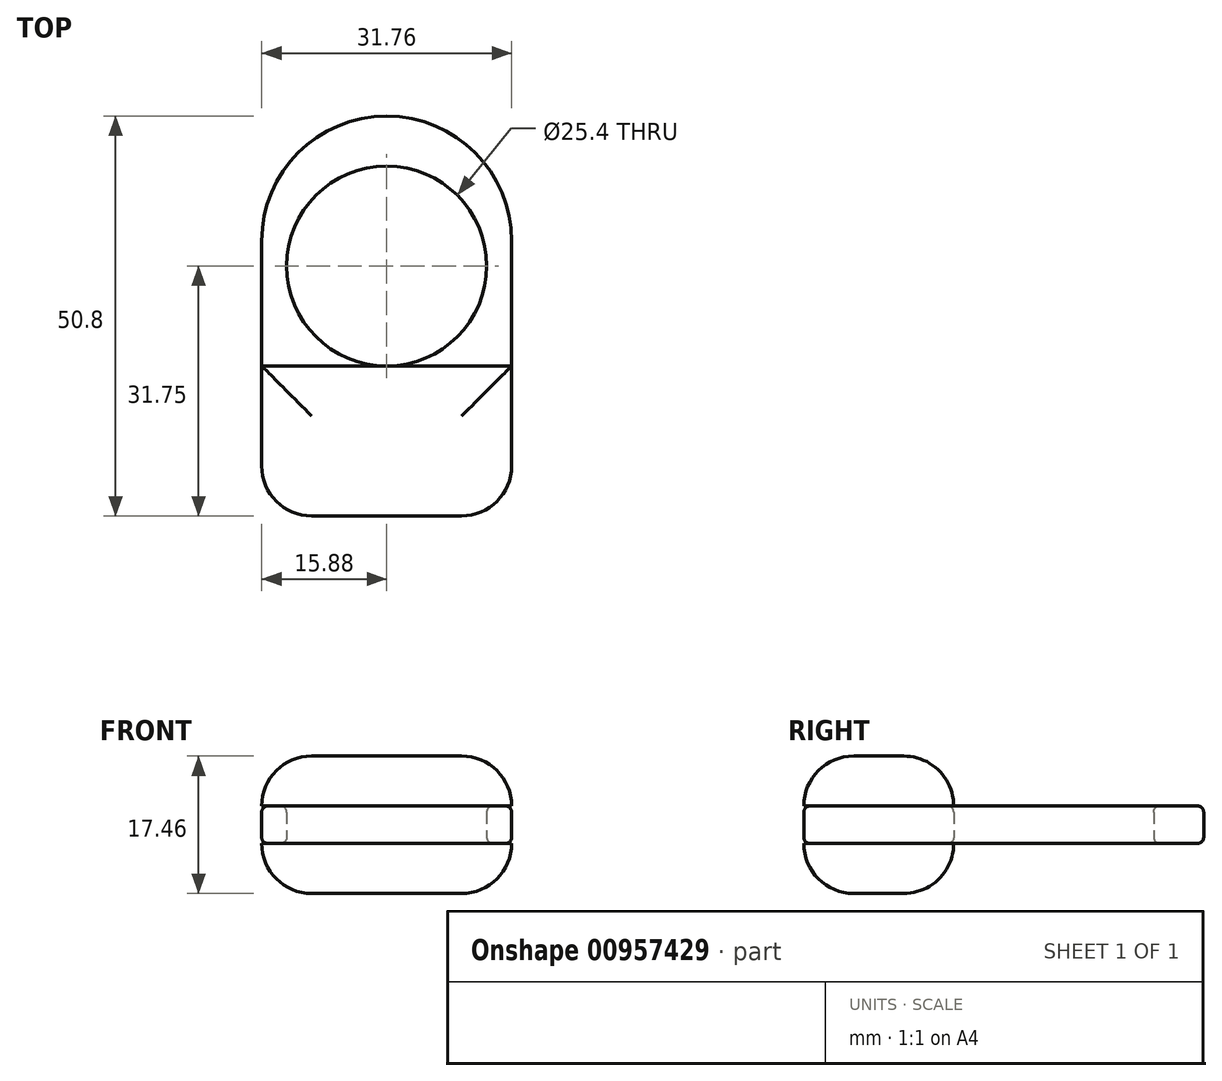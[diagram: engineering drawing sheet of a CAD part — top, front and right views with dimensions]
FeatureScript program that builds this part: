
annotation { "Feature Type Name" : "Feature", "Feature Type Description" : "" }
export const myFeature = defineFeature(function(context is Context, id is Id, definition is map)
    precondition{}
    {
        {
            var Q0;
            Q0=qCreatedBy(makeId("Top.planeOp"),FACE);
            var sketch = newSketch(context, id + "F0", { "sketchPlane" : qUnion([Q0])});
            skLineSegment(sketch, "E0.bottom", {"start": v(9.53, -25.4) * mm, "end": v(-9.52, -25.4) * mm});
            skLineSegment(sketch, "E0.top", {"start": v(15.87, 25.4) * mm, "end": v(-15.88, 25.4) * mm, "construction": true});
            skLineSegment(sketch, "E0.left", {"start": v(15.88, -19.05) * mm, "end": v(15.87, 25.4) * mm});
            skLineSegment(sketch, "E0.right", {"start": v(-15.87, -19.05) * mm, "end": v(-15.88, 25.4) * mm});
            skPoint(sketch, "E0.middle", {"position": v(0, 0) * mm});
            skCircle(sketch, "E1", {"center": v(0, 6.35) * mm, "radius": 12.7 * mm});
            skPoint(sketch, "E2.visualSharp", {"position": v(-15.87, -25.4) * mm});
            skArc(sketch, "E2.filletArc", {"start": v(-15.87, -19.05) * mm, "mid": v(-14.02, -23.54) * mm, "end": v(-9.52, -25.4) * mm});
            skPoint(sketch, "E3.visualSharp", {"position": v(15.88, -25.4) * mm});
            skArc(sketch, "E3.filletArc", {"start": v(9.53, -25.4) * mm, "mid": v(14.02, -23.54) * mm, "end": v(15.88, -19.05) * mm});
            skArc(sketch, "E4", {"start": v(-15.87, 9.53) * mm, "mid": v(0, 25.4) * mm, "end": v(15.87, 9.53) * mm});
            skSolve(sketch);
        }
        {
            var Q0;
            Q0 = qSketchRegion(id + "F0", true);
            extrude(context, id + "F1", {"entities" : qUnion([Q0]), "depth" : 4.76 * mm, "offsetDistance" : 25.4 * mm});
        }
        {
            var Q0;
            Q0=makeQuery(id+"F1.opExtrude","CAP_FACE",FACE,{"disambiguationData":[OSD([sQuery(id+"F0.wireOp",EDGE,"E0.bottom"),sQuery(id+"F0.wireOp",EDGE,"E0.left"),sQuery(id+"F0.wireOp",EDGE,"E0.right"),sQuery(id+"F0.wireOp",EDGE,"E1"),sQuery(id+"F0.wireOp",EDGE,"E2.filletArc"),sQuery(id+"F0.wireOp",EDGE,"E3.filletArc"),sQuery(id+"F0.wireOp",EDGE,"E4")])],"isStart":false});
            var sketch = newSketch(context, id + "F2", { "sketchPlane" : qUnion([Q0])});
            skLineSegment(sketch, "E5", {"start": v(0, -6.35) * mm, "end": v(-15.88, -6.35) * mm});
            skPoint(sketch, "E5.endSnap0", {"position": v(-15.88, -4.76) * mm});
            skLineSegment(sketch, "E6", {"start": v(0, -6.35) * mm, "end": v(15.88, -6.35) * mm});
            skSolve(sketch);
        }
        {
            var Q0;
            {var subQ2=sQuery(id+"F2.wireOp",EDGE,"E5");Q0=makeQuery(id+"F2.imprint","IMPRINT",FACE,{"disambiguationData":[TD([[makeQuery(id+"F2.imprint","IMPRINT",EDGE,{"derivedFrom":subQ2}),1.0]])]});}
            extrude(context, id + "F3", {"entities" : qUnion([Q0]), "depth" : 6.35 * mm, "offsetDistance" : 25.4 * mm});
        }
        {
            var Q0;
            Q0=makeQuery(id+"F1.opExtrude","CAP_FACE",FACE,{"disambiguationData":[OSD([sQuery(id+"F0.wireOp",EDGE,"E0.bottom"),sQuery(id+"F0.wireOp",EDGE,"E0.left"),sQuery(id+"F0.wireOp",EDGE,"E0.right"),sQuery(id+"F0.wireOp",EDGE,"E1"),sQuery(id+"F0.wireOp",EDGE,"E2.filletArc"),sQuery(id+"F0.wireOp",EDGE,"E3.filletArc"),sQuery(id+"F0.wireOp",EDGE,"E4")])],"isStart":true});
            var sketch = newSketch(context, id + "F4", { "sketchPlane" : qUnion([Q0])});
            skLineSegment(sketch, "E7", {"start": v(0, 6.35) * mm, "end": v(-15.88, 6.35) * mm});
            skPoint(sketch, "E7.endSnap0", {"position": v(-15.88, 4.76) * mm});
            skLineSegment(sketch, "E8", {"start": v(0, 6.35) * mm, "end": v(15.88, 6.35) * mm});
            skSolve(sketch);
        }
        {
            var Q0;
            {var subQ2=sQuery(id+"F4.wireOp",EDGE,"E7");Q0=makeQuery(id+"F4.imprint","IMPRINT",FACE,{"disambiguationData":[TD([[makeQuery(id+"F4.imprint","IMPRINT",EDGE,{"derivedFrom":subQ2}),-1.0]])]});}
            extrude(context, id + "F5", {"entities" : qUnion([Q0]), "depth" : 6.35 * mm, "offsetDistance" : 25.4 * mm});
        }
        {
            var Q0;
            Q0=makeQuery(id+"F5.opExtrude","CAP_FACE",FACE,{"disambiguationData":[OSD([sQuery(id+"F0.wireOp",EDGE,"E0.bottom"),sQuery(id+"F0.wireOp",EDGE,"E0.left"),sQuery(id+"F0.wireOp",EDGE,"E0.right"),sQuery(id+"F0.wireOp",EDGE,"E2.filletArc"),sQuery(id+"F0.wireOp",EDGE,"E3.filletArc"),sQuery(id+"F4.wireOp",EDGE,"E7"),sQuery(id+"F4.wireOp",EDGE,"E8")])],"isStart":false});
            var Q1;
            Q1=makeQuery(id+"F3.opExtrude","CAP_FACE",FACE,{"disambiguationData":[OSD([sQuery(id+"F0.wireOp",EDGE,"E0.bottom"),sQuery(id+"F0.wireOp",EDGE,"E0.left"),sQuery(id+"F0.wireOp",EDGE,"E0.right"),sQuery(id+"F0.wireOp",EDGE,"E2.filletArc"),sQuery(id+"F0.wireOp",EDGE,"E3.filletArc"),sQuery(id+"F2.wireOp",EDGE,"E5"),sQuery(id+"F2.wireOp",EDGE,"E6")])],"isStart":false});
            fillet(context, id + "F6", {"entities" : qUnion([Q0, Q1]), "radius" : 6.35 * mm, "tangentPropagation" : true, "allowEdgeOverflow" : false});
        }
        {
            var Q0;
            Q0=makeQuery(id+"F1.opExtrude","CAP_FACE",FACE,{"disambiguationData":[OSD([sQuery(id+"F0.wireOp",EDGE,"E0.bottom"),sQuery(id+"F0.wireOp",EDGE,"E0.left"),sQuery(id+"F0.wireOp",EDGE,"E0.right"),sQuery(id+"F0.wireOp",EDGE,"E1"),sQuery(id+"F0.wireOp",EDGE,"E2.filletArc"),sQuery(id+"F0.wireOp",EDGE,"E3.filletArc"),sQuery(id+"F0.wireOp",EDGE,"E4")])],"isStart":false});
            var Q1;
            Q1=makeQuery(id+"F1.opExtrude","CAP_FACE",FACE,{"disambiguationData":[OSD([sQuery(id+"F0.wireOp",EDGE,"E0.bottom"),sQuery(id+"F0.wireOp",EDGE,"E0.left"),sQuery(id+"F0.wireOp",EDGE,"E0.right"),sQuery(id+"F0.wireOp",EDGE,"E1"),sQuery(id+"F0.wireOp",EDGE,"E2.filletArc"),sQuery(id+"F0.wireOp",EDGE,"E3.filletArc"),sQuery(id+"F0.wireOp",EDGE,"E4")])],"isStart":true});
            fillet(context, id + "F7", {"entities" : qUnion([Q0, Q1]), "radius" : 0.8 * mm, "tangentPropagation" : true, "allowEdgeOverflow" : false});
        }
    });
